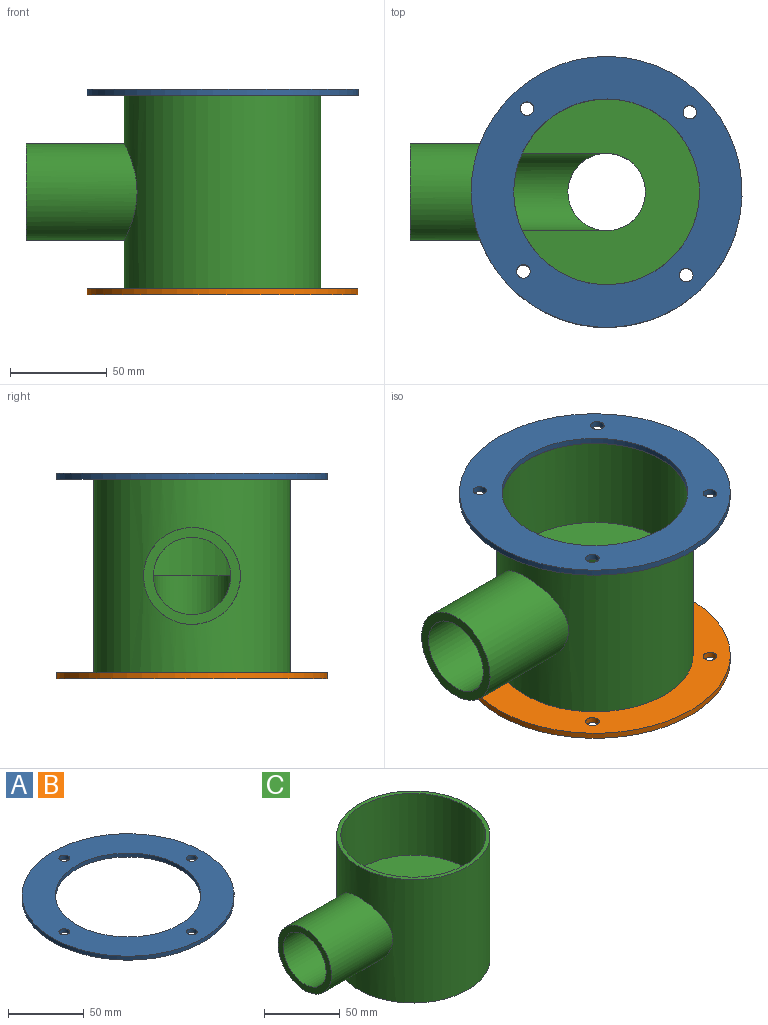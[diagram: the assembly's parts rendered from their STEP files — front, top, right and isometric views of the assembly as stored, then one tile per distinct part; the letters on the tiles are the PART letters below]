
ASSEMBLY  parts=3 mates=2
PART A: 8 faces, bbox 140x140x3.2 mm
  f0: cylinder r=3.5mm len=7mm, axis (0,0,-1), area 69.8mm2, adj f6,f7
  f1: cylinder r=3.5mm len=7mm, axis (0,0,-1), area 69.8mm2, adj f6,f7
  f2: cylinder r=3.5mm len=7mm, axis (0,0,-1), area 69.8mm2, adj f6,f7
  f3: cylinder r=3.5mm len=7mm, axis (0,0,-1), area 69.8mm2, adj f6,f7
  f4: cylinder r=48mm len=96mm, axis (0,0,-1), area 957.6mm2, adj f6,f7
  f5: cylinder r=70mm len=140mm, axis (0,0,-1), area 1396.4mm2, adj f6,f7
  f6: plane 140x140mm, normal (0,0,1), area 8001.6mm2, adj f0,f1,f2,f3,f4,f5
  f7: plane 140x140mm, normal (0,0,-1), area 8001.6mm2, adj f0,f1,f2,f3,f4,f5
PART B: same geometry as A
PART C: 9 faces, bbox 152.4x101.6x100 mm
  f0: cylinder r=48mm len=96mm, axis (0,0,-1), area 14436.7mm2, adj f2,f4,f6
  f1: cylinder r=50.8mm len=101.6mm, axis (0,0,-1), area 29889.9mm2, adj f2,f3,f8
  f2: plane 101.6x101.6mm, normal (0,0,1), area 869.1mm2, adj f0,f1
  f3: plane 101.6x101.6mm, normal (0,0,-1), area 6850.4mm2, adj f1,f5
  f4: plane 96x91.64mm, normal (0,0,1), area 4746.9mm2, adj f0,f5,f6
  f5: cylinder r=20mm len=50mm, axis (0,0,1), area 5484.3mm2, adj f3,f4,f6
  f6: cylinder r=20mm len=101.28mm, axis (1,0,0), area 9086.6mm2, adj f0,f4,f5,f7
  f7: plane 50x50mm, normal (-1,0,0), area 706.9mm2, adj f6,f8
  f8: cylinder r=25mm len=57.38mm, axis (-1,0,0), area 8487.7mm2, adj f1,f7
PLACE A rot(axis=(0.37,-0.93,0),180deg) t=(0,0,51.59)mm
PLACE B rot(axis=(0,0,-1),46.2deg) t=(0,0,-51.59)mm
PLACE C at identity fixed
MATE revolute A.f4 <-> C.f0  axis (0,0,-1) through (0,0,50)mm
MATE revolute B.f4 <-> C.f0  axis (0,0,1) through (0,0,-50)mm
